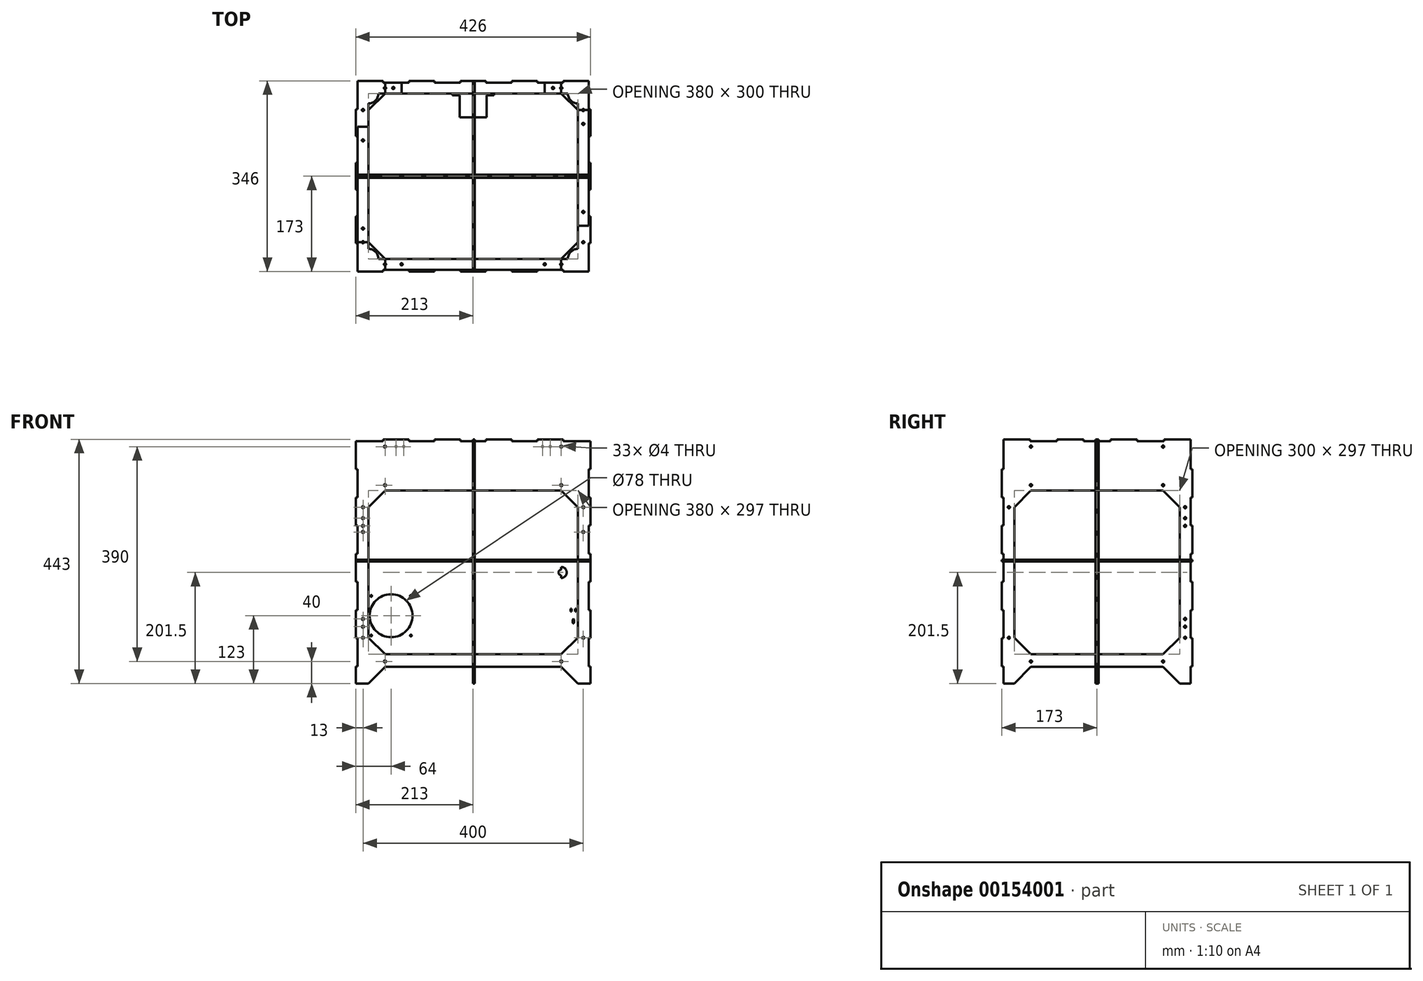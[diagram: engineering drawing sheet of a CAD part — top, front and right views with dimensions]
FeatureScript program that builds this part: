
annotation { "Feature Type Name" : "Feature", "Feature Type Description" : "" }
export const myFeature = defineFeature(function(context is Context, id is Id, definition is map)
    precondition{}
    {
        {
            assignVariable(context, id + "F0", {"name" : "thick", "anyValue" : 3});
        }
        {
            var Q0;
            Q0=qCreatedBy(makeId("Top.planeOp"),FACE);
            var sketch = newSketch(context, id + "F1", { "sketchPlane" : qUnion([Q0])});
            skLineSegment(sketch, "E0.bottom", {"start": v(213, -173) * mm, "end": v(-213, -173) * mm});
            skLineSegment(sketch, "E0.top", {"start": v(213, 173) * mm, "end": v(-213, 173) * mm});
            skLineSegment(sketch, "E0.left", {"start": v(213, -173) * mm, "end": v(213, 173) * mm});
            skLineSegment(sketch, "E0.right", {"start": v(-213, -173) * mm, "end": v(-213, 173) * mm});
            skPoint(sketch, "E0.middle", {"position": v(0, 0) * mm});
            skLineSegment(sketch, "E1.bottom", {"start": v(160, -150) * mm, "end": v(-160, -150) * mm});
            skLineSegment(sketch, "E1.top", {"start": v(160, 150) * mm, "end": v(-160, 150) * mm});
            skLineSegment(sketch, "E1.left", {"start": v(190, -120) * mm, "end": v(190, 120) * mm});
            skLineSegment(sketch, "E1.right", {"start": v(-190, -120) * mm, "end": v(-190, 120) * mm});
            skLineSegment(sketch, "E2", {"start": v(-160, 150) * mm, "end": v(-190, 120) * mm});
            skLineSegment(sketch, "E3", {"start": v(-190, -120) * mm, "end": v(-160, -150) * mm});
            skLineSegment(sketch, "E4", {"start": v(190, -120) * mm, "end": v(160, -150) * mm});
            skLineSegment(sketch, "E5", {"start": v(190, 120) * mm, "end": v(160, 150) * mm});
            skPoint(sketch, "E6.orphan", {"position": v(-190, 150) * mm});
            skPoint(sketch, "E7.orphan", {"position": v(-190, -150) * mm});
            skPoint(sketch, "E8.orphan", {"position": v(190, -150) * mm});
            skPoint(sketch, "E9.orphan", {"position": v(190, 150) * mm});
            skCircle(sketch, "E10", {"center": v(-160, 160) * mm, "radius": 2 * mm});
            skCircle(sketch, "E11", {"center": v(160, 160) * mm, "radius": 2 * mm});
            skCircle(sketch, "E12", {"center": v(-200, 120) * mm, "radius": 2 * mm});
            skCircle(sketch, "E13", {"center": v(-200, -120) * mm, "radius": 2 * mm});
            skCircle(sketch, "E14", {"center": v(-160, -160) * mm, "radius": 2 * mm});
            skCircle(sketch, "E15", {"center": v(160, -160) * mm, "radius": 2 * mm});
            skCircle(sketch, "E16", {"center": v(200, -120) * mm, "radius": 2 * mm});
            skCircle(sketch, "E17", {"center": v(200, 120) * mm, "radius": 2 * mm});
            skLineSegment(sketch, "E18", {"start": v(-163.33, -173) * mm, "end": v(-163.33, -170) * mm});
            skLineSegment(sketch, "E19", {"start": v(-163.33, -170) * mm, "end": v(-116.67, -170) * mm});
            skLineSegment(sketch, "E20", {"start": v(-116.67, -170) * mm, "end": v(-116.67, -173) * mm});
            skLineSegment(sketch, "E21.1.0.0", {"start": v(-70, -173) * mm, "end": v(-70, -170) * mm});
            skLineSegment(sketch, "E21.1.0.1", {"start": v(-70, -170) * mm, "end": v(-23.33, -170) * mm});
            skLineSegment(sketch, "E21.1.0.2", {"start": v(-23.33, -170) * mm, "end": v(-23.33, -173) * mm});
            skLineSegment(sketch, "E21.2.0.0", {"start": v(23.33, -173) * mm, "end": v(23.33, -170) * mm});
            skLineSegment(sketch, "E21.2.0.1", {"start": v(23.33, -170) * mm, "end": v(70, -170) * mm});
            skLineSegment(sketch, "E21.2.0.2", {"start": v(70, -170) * mm, "end": v(70, -173) * mm});
            skLineSegment(sketch, "E21.3.0.0", {"start": v(116.67, -173) * mm, "end": v(116.67, -170) * mm});
            skLineSegment(sketch, "E21.3.0.1", {"start": v(116.67, -170) * mm, "end": v(163.33, -170) * mm});
            skLineSegment(sketch, "E21.3.0.2", {"start": v(163.33, -170) * mm, "end": v(163.33, -173) * mm});
            skLineSegment(sketch, "E21.direction1", {"start": v(-163.33, -173) * mm, "end": v(-70, -173) * mm, "construction": true});
            skLineSegment(sketch, "E22", {"start": v(-163.33, 173) * mm, "end": v(-163.33, 170) * mm});
            skLineSegment(sketch, "E23", {"start": v(-163.33, 170) * mm, "end": v(-116.67, 170) * mm});
            skLineSegment(sketch, "E24", {"start": v(-116.67, 170) * mm, "end": v(-116.67, 173) * mm});
            skLineSegment(sketch, "E25.1.0.0", {"start": v(-70, 173) * mm, "end": v(-70, 170) * mm});
            skLineSegment(sketch, "E25.1.0.1", {"start": v(-70, 170) * mm, "end": v(-23.33, 170) * mm});
            skLineSegment(sketch, "E25.1.0.2", {"start": v(-23.33, 170) * mm, "end": v(-23.33, 173) * mm});
            skLineSegment(sketch, "E25.2.0.0", {"start": v(23.33, 173) * mm, "end": v(23.33, 170) * mm});
            skLineSegment(sketch, "E25.2.0.1", {"start": v(23.33, 170) * mm, "end": v(70, 170) * mm});
            skLineSegment(sketch, "E25.2.0.2", {"start": v(70, 170) * mm, "end": v(70, 173) * mm});
            skLineSegment(sketch, "E25.3.0.0", {"start": v(116.67, 173) * mm, "end": v(116.67, 170) * mm});
            skLineSegment(sketch, "E25.3.0.1", {"start": v(116.67, 170) * mm, "end": v(163.33, 170) * mm});
            skLineSegment(sketch, "E25.3.0.2", {"start": v(163.33, 170) * mm, "end": v(163.33, 173) * mm});
            skLineSegment(sketch, "E25.direction1", {"start": v(-163.33, 170) * mm, "end": v(-70, 170) * mm, "construction": true});
            skLineSegment(sketch, "E26", {"start": v(-213, -121.43) * mm, "end": v(-210, -121.43) * mm});
            skLineSegment(sketch, "E27", {"start": v(-210, -121.43) * mm, "end": v(-210, -170) * mm});
            skLineSegment(sketch, "E28", {"start": v(-210, -170) * mm, "end": v(-213, -170) * mm});
            skLineSegment(sketch, "E29.0.1.0", {"start": v(-213, -24.29) * mm, "end": v(-210, -24.29) * mm});
            skLineSegment(sketch, "E29.0.1.1", {"start": v(-210, -24.29) * mm, "end": v(-210, -72.86) * mm});
            skLineSegment(sketch, "E29.0.1.2", {"start": v(-210, -72.86) * mm, "end": v(-213, -72.86) * mm});
            skLineSegment(sketch, "E29.0.2.0", {"start": v(-213, 72.86) * mm, "end": v(-210, 72.86) * mm});
            skLineSegment(sketch, "E29.0.2.1", {"start": v(-210, 72.86) * mm, "end": v(-210, 24.29) * mm});
            skLineSegment(sketch, "E29.0.2.2", {"start": v(-210, 24.29) * mm, "end": v(-213, 24.29) * mm});
            skLineSegment(sketch, "E29.0.3.0", {"start": v(-213, 170) * mm, "end": v(-210, 170) * mm});
            skLineSegment(sketch, "E29.0.3.1", {"start": v(-210, 170) * mm, "end": v(-210, 121.43) * mm});
            skLineSegment(sketch, "E29.0.3.2", {"start": v(-210, 121.43) * mm, "end": v(-213, 121.43) * mm});
            skLineSegment(sketch, "E29.direction1", {"start": v(-213, -121.43) * mm, "end": v(-188, -121.43) * mm, "construction": true});
            skLineSegment(sketch, "E29.direction2", {"start": v(-213, -121.43) * mm, "end": v(-213, -24.29) * mm, "construction": true});
            skLineSegment(sketch, "E30", {"start": v(-210, -173) * mm, "end": v(-210, -170) * mm});
            skLineSegment(sketch, "E31", {"start": v(-210, 173) * mm, "end": v(-210, 170) * mm});
            skLineSegment(sketch, "E32", {"start": v(210, -173) * mm, "end": v(210, -170) * mm});
            skLineSegment(sketch, "E33", {"start": v(210, 173) * mm, "end": v(210, 170) * mm});
            skLineSegment(sketch, "E34", {"start": v(213, -170) * mm, "end": v(210, -170) * mm});
            skLineSegment(sketch, "E35", {"start": v(210, -170) * mm, "end": v(210, -121.43) * mm});
            skLineSegment(sketch, "E36", {"start": v(210, -121.43) * mm, "end": v(213, -121.43) * mm});
            skLineSegment(sketch, "E37.0.1.0", {"start": v(210, -24.29) * mm, "end": v(213, -24.29) * mm});
            skLineSegment(sketch, "E37.0.1.1", {"start": v(210, -72.86) * mm, "end": v(210, -24.29) * mm});
            skLineSegment(sketch, "E37.0.1.2", {"start": v(213, -72.86) * mm, "end": v(210, -72.86) * mm});
            skLineSegment(sketch, "E37.0.2.0", {"start": v(210, 72.86) * mm, "end": v(213, 72.86) * mm});
            skLineSegment(sketch, "E37.0.2.1", {"start": v(210, 24.29) * mm, "end": v(210, 72.86) * mm});
            skLineSegment(sketch, "E37.0.2.2", {"start": v(213, 24.29) * mm, "end": v(210, 24.29) * mm});
            skLineSegment(sketch, "E37.0.3.0", {"start": v(210, 170) * mm, "end": v(213, 170) * mm});
            skLineSegment(sketch, "E37.0.3.1", {"start": v(210, 121.43) * mm, "end": v(210, 170) * mm});
            skLineSegment(sketch, "E37.0.3.2", {"start": v(213, 121.43) * mm, "end": v(210, 121.43) * mm});
            skLineSegment(sketch, "E37.direction1", {"start": v(210, -121.43) * mm, "end": v(235, -121.43) * mm, "construction": true});
            skLineSegment(sketch, "E37.direction2", {"start": v(210, -121.43) * mm, "end": v(210, -24.29) * mm, "construction": true});
            skCircle(sketch, "E38", {"center": v(-140, 160) * mm, "radius": 2 * mm, "construction": true});
            skCircle(sketch, "E39", {"center": v(-126, 160) * mm, "radius": 2 * mm, "construction": true});
            skCircle(sketch, "E40", {"center": v(140, 160) * mm, "radius": 2 * mm, "construction": true});
            skCircle(sketch, "E41", {"center": v(126, 160) * mm, "radius": 2 * mm, "construction": true});
            skPoint(sketch, "E42.centerSnap0", {"position": v(-210, 48.57) * mm});
            skSolve(sketch);
        }
        {
            var Q0;
            Q0=makeQuery(id+"F1.imprint","IMPRINT",FACE,{"disambiguationData":[TD([[makeQuery(id+"F1.imprint","IMPRINT",EDGE,{"derivedFrom":sQuery(id+"F1.wireOp",EDGE,"E0.bottom")}),-1.0]])]});
            extrude(context, id + "F2", {"entities" : qUnion([Q0]), "depth" : (getVariable(context, 'thick')) * mm});
        }
        {
            var Q0;
            Q0=qCreatedBy(makeId("Front.planeOp"),FACE);
            var sketch = newSketch(context, id + "F3", { "sketchPlane" : qUnion([Q0])});
            skLineSegment(sketch, "E43.bottom", {"start": v(213, -221.5) * mm, "end": v(190, -221.5) * mm});
            skLineSegment(sketch, "E43.top", {"start": v(213, 221.5) * mm, "end": v(-213, 221.5) * mm});
            skLineSegment(sketch, "E43.left", {"start": v(213, -221.5) * mm, "end": v(213, 221.5) * mm});
            skLineSegment(sketch, "E43.right", {"start": v(-213, -221.5) * mm, "end": v(-213, 221.5) * mm});
            skPoint(sketch, "E43.middle", {"position": v(0, 0) * mm});
            skLineSegment(sketch, "E44.bottom", {"start": v(160, 128.5) * mm, "end": v(-160, 128.5) * mm});
            skLineSegment(sketch, "E44.top", {"start": v(160, -168.5) * mm, "end": v(-160, -168.5) * mm});
            skLineSegment(sketch, "E44.left", {"start": v(190, 98.5) * mm, "end": v(190, -138.5) * mm});
            skLineSegment(sketch, "E44.right", {"start": v(-190, 98.5) * mm, "end": v(-190, -138.5) * mm});
            skPoint(sketch, "E44.middle", {"position": v(0, -20) * mm});
            skLineSegment(sketch, "E45", {"start": v(-160, 128.5) * mm, "end": v(-190, 98.5) * mm});
            skLineSegment(sketch, "E46", {"start": v(-190, -138.5) * mm, "end": v(-160, -168.5) * mm});
            skLineSegment(sketch, "E47", {"start": v(190, -138.5) * mm, "end": v(160, -168.5) * mm});
            skLineSegment(sketch, "E48", {"start": v(160, 128.5) * mm, "end": v(190, 98.5) * mm});
            skPoint(sketch, "E49.orphan", {"position": v(-190, 128.5) * mm});
            skPoint(sketch, "E50.orphan", {"position": v(-190, -168.5) * mm});
            skPoint(sketch, "E51.orphan", {"position": v(190, 128.5) * mm});
            skPoint(sketch, "E52.orphan", {"position": v(190, -168.5) * mm});
            skLineSegment(sketch, "E53", {"start": v(-190, -221.5) * mm, "end": v(-160, -191.5) * mm});
            skLineSegment(sketch, "E54", {"start": v(-160, -191.5) * mm, "end": v(160, -191.5) * mm});
            skLineSegment(sketch, "E55", {"start": v(160, -191.5) * mm, "end": v(190, -221.5) * mm});
            skLineSegment(sketch, "E56.trimOffspring", {"start": v(-190, -221.5) * mm, "end": v(-213, -221.5) * mm});
            skCircle(sketch, "E57", {"center": v(-160, 208.5) * mm, "radius": 2 * mm});
            skCircle(sketch, "E58", {"center": v(160, 208.5) * mm, "radius": 2 * mm});
            skCircle(sketch, "E59", {"center": v(-160, 138.5) * mm, "radius": 2 * mm});
            skCircle(sketch, "E60", {"center": v(160, 138.5) * mm, "radius": 2 * mm});
            skCircle(sketch, "E61", {"center": v(200, 98.5) * mm, "radius": 2 * mm});
            skCircle(sketch, "E62", {"center": v(-200, 98.5) * mm, "radius": 2 * mm});
            skCircle(sketch, "E63", {"center": v(200, -138.5) * mm, "radius": 2 * mm});
            skCircle(sketch, "E64", {"center": v(160, -181.5) * mm, "radius": 2 * mm});
            skCircle(sketch, "E65", {"center": v(-160, -181.5) * mm, "radius": 2 * mm});
            skCircle(sketch, "E66", {"center": v(-200, -138.5) * mm, "radius": 2 * mm});
            skCircle(sketch, "E67", {"center": v(-200, 78.5) * mm, "radius": 2 * mm});
            skCircle(sketch, "E68", {"center": v(-200, 64.5) * mm, "radius": 2 * mm});
            skCircle(sketch, "E69", {"center": v(-200, -118.5) * mm, "radius": 2 * mm});
            skCircle(sketch, "E70", {"center": v(-200, -104.5) * mm, "radius": 2 * mm});
            skLineSegment(sketch, "E71", {"start": v(-210, 221.5) * mm, "end": v(-210, 218.5) * mm});
            skLineSegment(sketch, "E72", {"start": v(-210, 218.5) * mm, "end": v(-163.33, 218.5) * mm});
            skLineSegment(sketch, "E73", {"start": v(-163.33, 218.5) * mm, "end": v(-163.33, 221.5) * mm});
            skLineSegment(sketch, "E74.1.0.0", {"start": v(-116.67, 221.5) * mm, "end": v(-116.67, 218.5) * mm});
            skLineSegment(sketch, "E74.1.0.1", {"start": v(-116.67, 218.5) * mm, "end": v(-70, 218.5) * mm});
            skLineSegment(sketch, "E74.1.0.2", {"start": v(-70, 218.5) * mm, "end": v(-70, 221.5) * mm});
            skLineSegment(sketch, "E74.2.0.0", {"start": v(-23.33, 221.5) * mm, "end": v(-23.33, 218.5) * mm});
            skLineSegment(sketch, "E74.2.0.1", {"start": v(-23.33, 218.5) * mm, "end": v(23.33, 218.5) * mm});
            skLineSegment(sketch, "E74.2.0.2", {"start": v(23.33, 218.5) * mm, "end": v(23.33, 221.5) * mm});
            skLineSegment(sketch, "E74.3.0.0", {"start": v(70, 221.5) * mm, "end": v(70, 218.5) * mm});
            skLineSegment(sketch, "E74.3.0.1", {"start": v(70, 218.5) * mm, "end": v(116.67, 218.5) * mm});
            skLineSegment(sketch, "E74.3.0.2", {"start": v(116.67, 218.5) * mm, "end": v(116.67, 221.5) * mm});
            skLineSegment(sketch, "E74.4.0.0", {"start": v(163.33, 221.5) * mm, "end": v(163.33, 218.5) * mm});
            skLineSegment(sketch, "E74.4.0.1", {"start": v(163.33, 218.5) * mm, "end": v(210, 218.5) * mm});
            skLineSegment(sketch, "E74.4.0.2", {"start": v(210, 218.5) * mm, "end": v(210, 221.5) * mm});
            skLineSegment(sketch, "E74.direction1", {"start": v(-210, 218.5) * mm, "end": v(-116.67, 218.5) * mm, "construction": true});
            skLineSegment(sketch, "E75", {"start": v(-213, 218.5) * mm, "end": v(-210, 218.5) * mm});
            skLineSegment(sketch, "E76", {"start": v(213, 218.5) * mm, "end": v(210, 218.5) * mm});
            skLineSegment(sketch, "E77", {"start": v(-213, -139.28) * mm, "end": v(-210, -139.28) * mm});
            skLineSegment(sketch, "E78", {"start": v(-210, -139.28) * mm, "end": v(-210, -190.39) * mm});
            skLineSegment(sketch, "E79", {"start": v(-210, -190.39) * mm, "end": v(-213, -190.39) * mm});
            skLineSegment(sketch, "E80.0.1.0", {"start": v(-210, -37.06) * mm, "end": v(-210, -88.17) * mm});
            skLineSegment(sketch, "E80.0.1.1", {"start": v(-213, -37.06) * mm, "end": v(-210, -37.06) * mm});
            skLineSegment(sketch, "E80.0.1.2", {"start": v(-210, -88.17) * mm, "end": v(-213, -88.17) * mm});
            skLineSegment(sketch, "E80.0.2.0", {"start": v(-210, 65.17) * mm, "end": v(-210, 14.06) * mm});
            skLineSegment(sketch, "E80.0.2.1", {"start": v(-213, 65.17) * mm, "end": v(-210, 65.17) * mm});
            skLineSegment(sketch, "E80.0.2.2", {"start": v(-210, 14.06) * mm, "end": v(-213, 14.06) * mm});
            skLineSegment(sketch, "E80.0.3.0", {"start": v(-210, 167.39) * mm, "end": v(-210, 116.28) * mm});
            skLineSegment(sketch, "E80.0.3.1", {"start": v(-213, 167.39) * mm, "end": v(-210, 167.39) * mm});
            skLineSegment(sketch, "E80.0.3.2", {"start": v(-210, 116.28) * mm, "end": v(-213, 116.28) * mm});
            skLineSegment(sketch, "E80.direction1", {"start": v(-210, -190.39) * mm, "end": v(-185.37, -190.39) * mm, "construction": true});
            skLineSegment(sketch, "E80.direction2", {"start": v(-210, -190.39) * mm, "end": v(-210, -88.17) * mm, "construction": true});
            skLineSegment(sketch, "E81", {"start": v(213, -190.39) * mm, "end": v(210, -190.39) * mm});
            skLineSegment(sketch, "E82", {"start": v(210, -190.39) * mm, "end": v(210, -139.28) * mm});
            skLineSegment(sketch, "E83", {"start": v(210, -139.28) * mm, "end": v(213, -139.28) * mm});
            skLineSegment(sketch, "E84.0.1.0", {"start": v(210, -37.06) * mm, "end": v(213, -37.06) * mm});
            skLineSegment(sketch, "E84.0.1.1", {"start": v(210, -88.17) * mm, "end": v(210, -37.06) * mm});
            skLineSegment(sketch, "E84.0.1.2", {"start": v(213, -88.17) * mm, "end": v(210, -88.17) * mm});
            skLineSegment(sketch, "E84.0.2.0", {"start": v(210, 65.17) * mm, "end": v(213, 65.17) * mm});
            skLineSegment(sketch, "E84.0.2.1", {"start": v(210, 14.06) * mm, "end": v(210, 65.17) * mm});
            skLineSegment(sketch, "E84.0.2.2", {"start": v(213, 14.06) * mm, "end": v(210, 14.06) * mm});
            skLineSegment(sketch, "E84.0.3.0", {"start": v(210, 167.39) * mm, "end": v(213, 167.39) * mm});
            skLineSegment(sketch, "E84.0.3.1", {"start": v(210, 116.28) * mm, "end": v(210, 167.39) * mm});
            skLineSegment(sketch, "E84.0.3.2", {"start": v(213, 116.28) * mm, "end": v(210, 116.28) * mm});
            skLineSegment(sketch, "E84.direction1", {"start": v(210, -139.28) * mm, "end": v(235, -139.28) * mm, "construction": true});
            skLineSegment(sketch, "E84.direction2", {"start": v(210, -139.28) * mm, "end": v(210, -37.06) * mm, "construction": true});
            skCircle(sketch, "E85", {"center": v(140, 208.5) * mm, "radius": 2 * mm});
            skCircle(sketch, "E86", {"center": v(126, 208.5) * mm, "radius": 2 * mm});
            skCircle(sketch, "E87", {"center": v(-140, 208.5) * mm, "radius": 2 * mm});
            skCircle(sketch, "E88", {"center": v(-126, 208.5) * mm, "radius": 2 * mm});
            skCircle(sketch, "E89", {"center": v(200, 53.5) * mm, "radius": 2 * mm});
            skArc(sketch, "E90", {"start": v(160, -10) * mm, "mid": v(170, -20) * mm, "end": v(160, -30) * mm});
            skArc(sketch, "E91", {"start": v(160, -15) * mm, "mid": v(155, -20) * mm, "end": v(160, -25) * mm});
            skLineSegment(sketch, "E92", {"start": v(160, -15) * mm, "end": v(160, -10) * mm});
            skLineSegment(sketch, "E93", {"start": v(160, -25) * mm, "end": v(160, -30) * mm});
            skCircle(sketch, "E94", {"center": v(-200, 53.5) * mm, "radius": 2 * mm});
            skLineSegment(sketch, "E95.bottom", {"start": v(-109, -58.5) * mm, "end": v(-189, -58.5) * mm, "construction": true});
            skLineSegment(sketch, "E95.top", {"start": v(-109, -138.5) * mm, "end": v(-189, -138.5) * mm, "construction": true});
            skLineSegment(sketch, "E95.left", {"start": v(-109, -58.5) * mm, "end": v(-109, -138.5) * mm, "construction": true});
            skLineSegment(sketch, "E95.right", {"start": v(-189, -58.5) * mm, "end": v(-189, -138.5) * mm, "construction": true});
            skPoint(sketch, "E95.middle", {"position": v(-149, -98.5) * mm});
            skCircle(sketch, "E96", {"center": v(-149, -98.5) * mm, "radius": 39 * mm});
            skLineSegment(sketch, "E97.bottom", {"start": v(-113, -62.5) * mm, "end": v(-185, -62.5) * mm, "construction": true});
            skLineSegment(sketch, "E97.top", {"start": v(-113, -134.5) * mm, "end": v(-185, -134.5) * mm, "construction": true});
            skLineSegment(sketch, "E97.left", {"start": v(-113, -62.5) * mm, "end": v(-113, -134.5) * mm, "construction": true});
            skLineSegment(sketch, "E97.right", {"start": v(-185, -62.5) * mm, "end": v(-185, -134.5) * mm, "construction": true});
            skCircle(sketch, "E98", {"center": v(-113, -62.5) * mm, "radius": 1.5 * mm});
            skCircle(sketch, "E99", {"center": v(-185, -62.5) * mm, "radius": 1.5 * mm});
            skCircle(sketch, "E100", {"center": v(-113, -134.5) * mm, "radius": 1.5 * mm});
            skCircle(sketch, "E101", {"center": v(-185, -134.5) * mm, "radius": 1.5 * mm});
            skEllipse(sketch, "E102", {"center": v(182, -108.5) * mm, "majorRadius": 4 * mm, "minorRadius": 1.5 * mm, "majorAxis": v(0, -1)});
            skLineSegment(sketch, "E103.bottom", {"start": v(177, -86) * mm, "end": v(179, -86) * mm});
            skLineSegment(sketch, "E103.top", {"start": v(177, -91) * mm, "end": v(179, -91) * mm});
            skLineSegment(sketch, "E103.left", {"start": v(177, -86) * mm, "end": v(177, -91) * mm});
            skLineSegment(sketch, "E103.right", {"start": v(179, -86) * mm, "end": v(179, -91) * mm});
            skLineSegment(sketch, "E104.bottom", {"start": v(185, -86) * mm, "end": v(187, -86) * mm});
            skLineSegment(sketch, "E104.top", {"start": v(185, -91) * mm, "end": v(187, -91) * mm});
            skLineSegment(sketch, "E104.left", {"start": v(185, -86) * mm, "end": v(185, -91) * mm});
            skLineSegment(sketch, "E104.right", {"start": v(187, -86) * mm, "end": v(187, -91) * mm});
            skPoint(sketch, "E105", {"position": v(182, -88.5) * mm});
            skPoint(sketch, "E106", {"position": v(179, -88.5) * mm});
            skPoint(sketch, "E107", {"position": v(185, -88.5) * mm});
            skSolve(sketch);
        }
        {
            var Q0;
            Q0=makeQuery(id+"F3.imprint","IMPRINT",FACE,{"disambiguationData":[TD([[makeQuery(id+"F3.imprint","IMPRINT",EDGE,{"derivedFrom":sQuery(id+"F3.wireOp",EDGE,"E43.bottom")}),-1.0]])]});
            var Q1;
            Q1=makeQuery(id+"F3.imprint","IMPRINT",FACE,{"disambiguationData":[TD([[makeQuery(id+"F3.imprint","IMPRINT",EDGE,{"derivedFrom":sQuery(id+"F3.wireOp",EDGE,"E87")}),1.0]])]});
            var Q2;
            Q2=makeQuery(id+"F3.imprint","IMPRINT",FACE,{"disambiguationData":[TD([[makeQuery(id+"F3.imprint","IMPRINT",EDGE,{"derivedFrom":sQuery(id+"F3.wireOp",EDGE,"E88")}),1.0]])]});
            var Q3;
            Q3=makeQuery(id+"F3.imprint","IMPRINT",FACE,{"disambiguationData":[TD([[makeQuery(id+"F3.imprint","IMPRINT",EDGE,{"derivedFrom":sQuery(id+"F3.wireOp",EDGE,"E86")}),1.0]])]});
            var Q4;
            Q4=makeQuery(id+"F3.imprint","IMPRINT",FACE,{"disambiguationData":[TD([[makeQuery(id+"F3.imprint","IMPRINT",EDGE,{"derivedFrom":sQuery(id+"F3.wireOp",EDGE,"E85")}),1.0]])]});
            extrude(context, id + "F4", {"entities" : qUnion([Q0, Q1, Q2, Q3, Q4]), "depth" : (getVariable(context, 'thick')) * mm});
        }
        {
            var Q0;
            Q0=makeQuery(id+"F3.imprint","IMPRINT",FACE,{"disambiguationData":[TD([[makeQuery(id+"F3.imprint","IMPRINT",EDGE,{"derivedFrom":sQuery(id+"F3.wireOp",EDGE,"E43.bottom")}),-1.0]])]});
            var Q1;
            Q1=makeQuery(id+"F3.imprint","IMPRINT",FACE,{"disambiguationData":[TD([[makeQuery(id+"F3.imprint","IMPRINT",EDGE,{"derivedFrom":sQuery(id+"F3.wireOp",EDGE,"E44.bottom")}),1.0]])]});
            var Q2;
            Q2=makeQuery(id+"F3.imprint","IMPRINT",FACE,{"disambiguationData":[TD([[makeQuery(id+"F3.imprint","IMPRINT",EDGE,{"derivedFrom":sQuery(id+"F3.wireOp",EDGE,"E67")}),1.0]])]});
            var Q3;
            Q3=makeQuery(id+"F3.imprint","IMPRINT",FACE,{"disambiguationData":[TD([[makeQuery(id+"F3.imprint","IMPRINT",EDGE,{"derivedFrom":sQuery(id+"F3.wireOp",EDGE,"E70")}),1.0]])]});
            var Q4;
            Q4=makeQuery(id+"F3.imprint","IMPRINT",FACE,{"disambiguationData":[TD([[makeQuery(id+"F3.imprint","IMPRINT",EDGE,{"derivedFrom":sQuery(id+"F3.wireOp",EDGE,"E69")}),1.0]])]});
            var Q5;
            Q5=makeQuery(id+"F3.imprint","IMPRINT",FACE,{"disambiguationData":[TD([[makeQuery(id+"F3.imprint","IMPRINT",EDGE,{"derivedFrom":sQuery(id+"F3.wireOp",EDGE,"E90")}),-1.0]])]});
            extrude(context, id + "F5", {"entities" : qUnion([Q0, Q1, Q2, Q3, Q4, Q5]), "oppositeDirection" : true, "depth" : (getVariable(context, 'thick')) * mm});
        }
        {
            var Q0;
            Q0=qCreatedBy(makeId("Right.planeOp"),FACE);
            var sketch = newSketch(context, id + "F6", { "sketchPlane" : qUnion([Q0])});
            skLineSegment(sketch, "E108.bottom", {"start": v(-173, -221.5) * mm, "end": v(173, -221.5) * mm});
            skLineSegment(sketch, "E108.top", {"start": v(-173, 221.5) * mm, "end": v(173, 221.5) * mm});
            skLineSegment(sketch, "E108.left", {"start": v(-173, -221.5) * mm, "end": v(-173, 221.5) * mm});
            skLineSegment(sketch, "E108.right", {"start": v(173, -221.5) * mm, "end": v(173, 221.5) * mm});
            skPoint(sketch, "E108.middle", {"position": v(0, 0) * mm});
            skLineSegment(sketch, "E109.bottom", {"start": v(-120, 128.5) * mm, "end": v(120, 128.5) * mm});
            skLineSegment(sketch, "E109.top", {"start": v(-120, -168.5) * mm, "end": v(120, -168.5) * mm});
            skLineSegment(sketch, "E109.left", {"start": v(-150, 98.5) * mm, "end": v(-150, -138.5) * mm});
            skLineSegment(sketch, "E109.right", {"start": v(150, 98.5) * mm, "end": v(150, -138.5) * mm});
            skPoint(sketch, "E109.middle", {"position": v(0, -20) * mm});
            skLineSegment(sketch, "E110", {"start": v(120, 128.5) * mm, "end": v(150, 98.5) * mm});
            skLineSegment(sketch, "E111", {"start": v(-120, 128.5) * mm, "end": v(-150, 98.5) * mm});
            skLineSegment(sketch, "E112", {"start": v(-150, -138.5) * mm, "end": v(-120, -168.5) * mm});
            skLineSegment(sketch, "E113", {"start": v(120, -168.5) * mm, "end": v(150, -138.5) * mm});
            skPoint(sketch, "E114.orphan", {"position": v(150, 128.5) * mm});
            skPoint(sketch, "E115.orphan", {"position": v(-150, 128.5) * mm});
            skPoint(sketch, "E116.orphan", {"position": v(-150, -168.5) * mm});
            skPoint(sketch, "E117.orphan", {"position": v(150, -168.5) * mm});
            skLineSegment(sketch, "E118", {"start": v(150, -221.5) * mm, "end": v(120, -191.5) * mm});
            skLineSegment(sketch, "E119", {"start": v(120, -191.5) * mm, "end": v(-120, -191.5) * mm});
            skLineSegment(sketch, "E120", {"start": v(-120, -191.5) * mm, "end": v(-150, -221.5) * mm});
            skCircle(sketch, "E121", {"center": v(120, 138.5) * mm, "radius": 2 * mm});
            skCircle(sketch, "E122", {"center": v(-120, 138.5) * mm, "radius": 2 * mm});
            skCircle(sketch, "E123", {"center": v(-120, 208.5) * mm, "radius": 2 * mm});
            skCircle(sketch, "E124", {"center": v(120, 208.5) * mm, "radius": 2 * mm});
            skCircle(sketch, "E125", {"center": v(160, 98.5) * mm, "radius": 2 * mm});
            skCircle(sketch, "E126", {"center": v(160, -138.5) * mm, "radius": 2 * mm});
            skCircle(sketch, "E127", {"center": v(-160, 98.5) * mm, "radius": 2 * mm});
            skCircle(sketch, "E128", {"center": v(-160, -138.5) * mm, "radius": 2 * mm});
            skCircle(sketch, "E129", {"center": v(120, -181.5) * mm, "radius": 2 * mm});
            skCircle(sketch, "E130", {"center": v(-120, -181.5) * mm, "radius": 2 * mm});
            skCircle(sketch, "E131", {"center": v(160, 78.5) * mm, "radius": 2 * mm});
            skCircle(sketch, "E132", {"center": v(160, 64.5) * mm, "radius": 2 * mm});
            skCircle(sketch, "E133", {"center": v(160, -118.5) * mm, "radius": 2 * mm});
            skCircle(sketch, "E134", {"center": v(160, -104.5) * mm, "radius": 2 * mm});
            skLineSegment(sketch, "E135", {"start": v(-170, 221.5) * mm, "end": v(-170, 218.5) * mm});
            skLineSegment(sketch, "E136", {"start": v(170, 221.5) * mm, "end": v(170, 218.5) * mm});
            skLineSegment(sketch, "E137", {"start": v(173, -241.5) * mm, "end": v(170, -241.5) * mm});
            skLineSegment(sketch, "E138", {"start": v(170, -241.5) * mm, "end": v(170, -190.39) * mm});
            skLineSegment(sketch, "E139", {"start": v(170, -190.39) * mm, "end": v(173, -190.39) * mm});
            skLineSegment(sketch, "E140", {"start": v(-173, -241.5) * mm, "end": v(-170, -241.5) * mm});
            skLineSegment(sketch, "E141", {"start": v(-170, -241.5) * mm, "end": v(-170, -190.39) * mm});
            skLineSegment(sketch, "E142", {"start": v(-170, -190.39) * mm, "end": v(-173, -190.39) * mm});
            skLineSegment(sketch, "E143.0.1.0", {"start": v(173, -139.28) * mm, "end": v(170, -139.28) * mm});
            skLineSegment(sketch, "E143.0.1.1", {"start": v(170, -139.28) * mm, "end": v(170, -88.17) * mm});
            skLineSegment(sketch, "E143.0.1.2", {"start": v(170, -88.17) * mm, "end": v(173, -88.17) * mm});
            skLineSegment(sketch, "E143.0.1.3", {"start": v(-170, -88.17) * mm, "end": v(-173, -88.17) * mm});
            skLineSegment(sketch, "E143.0.1.4", {"start": v(-170, -139.28) * mm, "end": v(-170, -88.17) * mm});
            skLineSegment(sketch, "E143.0.1.5", {"start": v(-173, -139.28) * mm, "end": v(-170, -139.28) * mm});
            skLineSegment(sketch, "E143.0.2.0", {"start": v(173, -37.06) * mm, "end": v(170, -37.06) * mm});
            skLineSegment(sketch, "E143.0.2.1", {"start": v(170, -37.06) * mm, "end": v(170, 14.06) * mm});
            skLineSegment(sketch, "E143.0.2.2", {"start": v(170, 14.06) * mm, "end": v(173, 14.06) * mm});
            skLineSegment(sketch, "E143.0.2.3", {"start": v(-170, 14.06) * mm, "end": v(-173, 14.06) * mm});
            skLineSegment(sketch, "E143.0.2.4", {"start": v(-170, -37.06) * mm, "end": v(-170, 14.06) * mm});
            skLineSegment(sketch, "E143.0.2.5", {"start": v(-173, -37.06) * mm, "end": v(-170, -37.06) * mm});
            skLineSegment(sketch, "E143.0.3.0", {"start": v(173, 65.17) * mm, "end": v(170, 65.17) * mm});
            skLineSegment(sketch, "E143.0.3.1", {"start": v(170, 65.17) * mm, "end": v(170, 116.28) * mm});
            skLineSegment(sketch, "E143.0.3.2", {"start": v(170, 116.28) * mm, "end": v(173, 116.28) * mm});
            skLineSegment(sketch, "E143.0.3.3", {"start": v(-170, 116.28) * mm, "end": v(-173, 116.28) * mm});
            skLineSegment(sketch, "E143.0.3.4", {"start": v(-170, 65.17) * mm, "end": v(-170, 116.28) * mm});
            skLineSegment(sketch, "E143.0.3.5", {"start": v(-173, 65.17) * mm, "end": v(-170, 65.17) * mm});
            skLineSegment(sketch, "E143.0.4.0", {"start": v(173, 167.39) * mm, "end": v(170, 167.39) * mm});
            skLineSegment(sketch, "E143.0.4.1", {"start": v(170, 167.39) * mm, "end": v(170, 218.5) * mm});
            skLineSegment(sketch, "E143.0.4.2", {"start": v(170, 218.5) * mm, "end": v(173, 218.5) * mm});
            skLineSegment(sketch, "E143.0.4.3", {"start": v(-170, 218.5) * mm, "end": v(-173, 218.5) * mm});
            skLineSegment(sketch, "E143.0.4.4", {"start": v(-170, 167.39) * mm, "end": v(-170, 218.5) * mm});
            skLineSegment(sketch, "E143.0.4.5", {"start": v(-173, 167.39) * mm, "end": v(-170, 167.39) * mm});
            skLineSegment(sketch, "E143.direction1", {"start": v(170, -241.5) * mm, "end": v(186.73, -241.5) * mm, "construction": true});
            skLineSegment(sketch, "E143.direction2", {"start": v(170, -241.5) * mm, "end": v(170, -139.28) * mm, "construction": true});
            skLineSegment(sketch, "E144", {"start": v(-72.86, 221.5) * mm, "end": v(-72.86, 218.5) * mm});
            skLineSegment(sketch, "E145", {"start": v(-72.86, 218.5) * mm, "end": v(-121.43, 218.5) * mm});
            skLineSegment(sketch, "E146", {"start": v(-121.43, 218.5) * mm, "end": v(-121.43, 221.5) * mm});
            skLineSegment(sketch, "E147.1.0.0", {"start": v(24.29, 221.5) * mm, "end": v(24.29, 218.5) * mm});
            skLineSegment(sketch, "E147.1.0.1", {"start": v(24.29, 218.5) * mm, "end": v(-24.29, 218.5) * mm});
            skLineSegment(sketch, "E147.1.0.2", {"start": v(-24.29, 218.5) * mm, "end": v(-24.29, 221.5) * mm});
            skLineSegment(sketch, "E147.2.0.0", {"start": v(121.43, 221.5) * mm, "end": v(121.43, 218.5) * mm});
            skLineSegment(sketch, "E147.2.0.1", {"start": v(121.43, 218.5) * mm, "end": v(72.86, 218.5) * mm});
            skLineSegment(sketch, "E147.2.0.2", {"start": v(72.86, 218.5) * mm, "end": v(72.86, 221.5) * mm});
            skLineSegment(sketch, "E147.direction1", {"start": v(-72.86, 218.5) * mm, "end": v(24.29, 218.5) * mm, "construction": true});
            skArc(sketch, "E148", {"start": v(-120, -10) * mm, "mid": v(-130, -20) * mm, "end": v(-120, -30) * mm});
            skArc(sketch, "E149", {"start": v(-120, -15) * mm, "mid": v(-115, -20) * mm, "end": v(-120, -25) * mm});
            skLineSegment(sketch, "E150", {"start": v(-120, -15) * mm, "end": v(-120, -10) * mm});
            skLineSegment(sketch, "E151", {"start": v(-120, -25) * mm, "end": v(-120, -30) * mm});
            skSolve(sketch);
        }
        {
            var Q0;
            Q0=makeQuery(id+"F6.imprint","IMPRINT",FACE,{"disambiguationData":[TD([[makeQuery(id+"F6.imprint","IMPRINT",EDGE,{"derivedFrom":sQuery(id+"F6.wireOp",EDGE,"E108.top")}),-1.0]])]});
            extrude(context, id + "F7", {"entities" : qUnion([Q0]), "depth" : (getVariable(context, 'thick')) * mm});
        }
        {
            var Q0;
            Q0=qCreatedBy(makeId("Top.planeOp"),FACE);
            var sketch = newSketch(context, id + "F8", { "sketchPlane" : qUnion([Q0])});
            skLineSegment(sketch, "E152.bottom", {"start": v(190, -150) * mm, "end": v(160, -150) * mm});
            skLineSegment(sketch, "E152.top", {"start": v(190, 150) * mm, "end": v(160, 150) * mm});
            skLineSegment(sketch, "E152.left", {"start": v(190, -150) * mm, "end": v(190, -90) * mm});
            skLineSegment(sketch, "E152.right", {"start": v(-190, -150) * mm, "end": v(-190, -120) * mm});
            skPoint(sketch, "E152.middle", {"position": v(0, 0) * mm});
            skLineSegment(sketch, "E153.bottom", {"start": v(-24.5, 150) * mm, "end": v(24.5, 150) * mm});
            skLineSegment(sketch, "E153.top", {"start": v(-24.5, 107) * mm, "end": v(24.5, 107) * mm});
            skLineSegment(sketch, "E153.left", {"start": v(-24.5, 147) * mm, "end": v(-24.5, 107) * mm});
            skLineSegment(sketch, "E153.right", {"start": v(24.5, 147) * mm, "end": v(24.5, 107) * mm});
            skLineSegment(sketch, "E154", {"start": v(0, 0) * mm, "end": v(0, 107) * mm, "construction": true});
            skLineSegment(sketch, "E155", {"start": v(-24.5, 147) * mm, "end": v(-37.5, 147) * mm});
            skLineSegment(sketch, "E156", {"start": v(-37.5, 147) * mm, "end": v(-37.5, 150) * mm});
            skLineSegment(sketch, "E157", {"start": v(24.5, 147) * mm, "end": v(37.5, 147) * mm});
            skLineSegment(sketch, "E158", {"start": v(37.5, 147) * mm, "end": v(37.5, 150) * mm});
            skLineSegment(sketch, "E159.bottom", {"start": v(-190, 90) * mm, "end": v(-210, 90) * mm});
            skLineSegment(sketch, "E159.top", {"start": v(-190, -120) * mm, "end": v(-210, -120) * mm});
            skLineSegment(sketch, "E159.right", {"start": v(-210, 90) * mm, "end": v(-210, -120) * mm});
            skLineSegment(sketch, "E160.bottom", {"start": v(190, 120) * mm, "end": v(210, 120) * mm});
            skLineSegment(sketch, "E160.top", {"start": v(190, -90) * mm, "end": v(210, -90) * mm});
            skLineSegment(sketch, "E160.right", {"start": v(210, 120) * mm, "end": v(210, -90) * mm});
            skLineSegment(sketch, "E161.top", {"start": v(-160, -170) * mm, "end": v(160, -170) * mm});
            skLineSegment(sketch, "E161.left", {"start": v(-160, -150) * mm, "end": v(-160, -170) * mm});
            skLineSegment(sketch, "E161.right", {"start": v(160, -150) * mm, "end": v(160, -170) * mm});
            skArc(sketch, "E162", {"start": v(190, -132) * mm, "mid": v(177.27, -137.27) * mm, "end": v(172, -150) * mm});
            skArc(sketch, "E163", {"start": v(-190, 132) * mm, "mid": v(-177.27, 137.27) * mm, "end": v(-172, 150) * mm});
            skArc(sketch, "E164", {"start": v(172, 150) * mm, "mid": v(177.27, 137.27) * mm, "end": v(190, 132) * mm});
            skCircle(sketch, "E165", {"center": v(200, 95) * mm, "radius": 2 * mm});
            skPoint(sketch, "E165.centerSnap0", {"position": v(200, 120) * mm});
            skCircle(sketch, "E166", {"center": v(200, -65) * mm, "radius": 2 * mm});
            skCircle(sketch, "E167", {"center": v(-200, -95) * mm, "radius": 2 * mm});
            skPoint(sketch, "E167.centerSnap0", {"position": v(-200, -120) * mm});
            skCircle(sketch, "E168", {"center": v(-200, 65) * mm, "radius": 2 * mm});
            skCircle(sketch, "E169", {"center": v(-130, -160) * mm, "radius": 2 * mm});
            skPoint(sketch, "E169.centerSnap0", {"position": v(-160, -160) * mm});
            skCircle(sketch, "E170", {"center": v(130, -160) * mm, "radius": 2 * mm});
            skLineSegment(sketch, "E171", {"start": v(-160, 150) * mm, "end": v(-160, 170) * mm});
            skLineSegment(sketch, "E172", {"start": v(-160, 170) * mm, "end": v(-130, 170) * mm});
            skLineSegment(sketch, "E173", {"start": v(-130, 170) * mm, "end": v(-130, 150) * mm});
            skLineSegment(sketch, "E174", {"start": v(160, 150) * mm, "end": v(160, 170) * mm});
            skLineSegment(sketch, "E175", {"start": v(160, 170) * mm, "end": v(130, 170) * mm});
            skLineSegment(sketch, "E176", {"start": v(130, 170) * mm, "end": v(130, 150) * mm});
            skCircle(sketch, "E177", {"center": v(-145, 160) * mm, "radius": 2 * mm});
            skPoint(sketch, "E177.centerSnap0", {"position": v(-130, 160) * mm});
            skPoint(sketch, "E177.centerSnap1", {"position": v(-145, 170) * mm});
            skCircle(sketch, "E178", {"center": v(145, 160) * mm, "radius": 2 * mm});
            skPoint(sketch, "E178.centerSnap0", {"position": v(145, 170) * mm});
            skPoint(sketch, "E178.centerSnap1", {"position": v(160, 160) * mm});
            skLineSegment(sketch, "E179.trimOffspring", {"start": v(130, 150) * mm, "end": v(-130, 150) * mm});
            skLineSegment(sketch, "E180.trimOffspring", {"start": v(-160, 150) * mm, "end": v(-190, 150) * mm});
            skLineSegment(sketch, "E181.trimOffspring", {"start": v(190, 120) * mm, "end": v(190, 150) * mm});
            skLineSegment(sketch, "E182.trimOffspring", {"start": v(-190, 90) * mm, "end": v(-190, 150) * mm});
            skLineSegment(sketch, "E183.trimOffspring", {"start": v(-160, -150) * mm, "end": v(-190, -150) * mm});
            skArc(sketch, "E184", {"start": v(-190, -132) * mm, "mid": v(-177.27, -137.27) * mm, "end": v(-172, -150) * mm});
            skSolve(sketch);
        }
        {
            var Q0;
            {var subQ11=sQuery(id+"F8.wireOp",EDGE,"E153.top");Q0=makeQuery(id+"F8.imprint","IMPRINT",FACE,{"disambiguationData":[TD([[makeQuery(id+"F8.imprint","IMPRINT",EDGE,{"derivedFrom":subQ11}),-1.0]])]});}
            var Q1;
            {var subQ0=sQuery(id+"F8.wireOp",EDGE,"E171");Q1=makeQuery(id+"F8.imprint","IMPRINT",FACE,{"disambiguationData":[TD([[makeQuery(id+"F8.imprint","IMPRINT",EDGE,{"derivedFrom":subQ0}),-1.0]])]});}
            var Q2;
            {var subQ1=sQuery(id+"F8.wireOp",EDGE,"E174");Q2=makeQuery(id+"F8.imprint","IMPRINT",FACE,{"disambiguationData":[TD([[makeQuery(id+"F8.imprint","IMPRINT",EDGE,{"derivedFrom":subQ1}),1.0]])]});}
            var Q3;
            Q3=makeQuery(id+"F8.imprint","IMPRINT",FACE,{"disambiguationData":[TD([[makeQuery(id+"F8.imprint","IMPRINT",EDGE,{"derivedFrom":sQuery(id+"F8.wireOp",EDGE,"E160.bottom")}),-1.0]])]});
            var Q4;
            Q4=makeQuery(id+"F8.imprint","IMPRINT",FACE,{"disambiguationData":[TD([[makeQuery(id+"F8.imprint","IMPRINT",EDGE,{"derivedFrom":sQuery(id+"F8.wireOp",EDGE,"E159.bottom")}),1.0]])]});
            var Q5;
            Q5=makeQuery(id+"F8.imprint","IMPRINT",FACE,{"disambiguationData":[TD([[makeQuery(id+"F8.imprint","IMPRINT",EDGE,{"derivedFrom":sQuery(id+"F8.wireOp",EDGE,"E161.bottom")}),-1.0]])]});
            extrude(context, id + "F9", {"entities" : qUnion([Q0, Q1, Q2, Q3, Q4, Q5]), "depth" : (getVariable(context, 'thick')) * mm});
        }
    });
